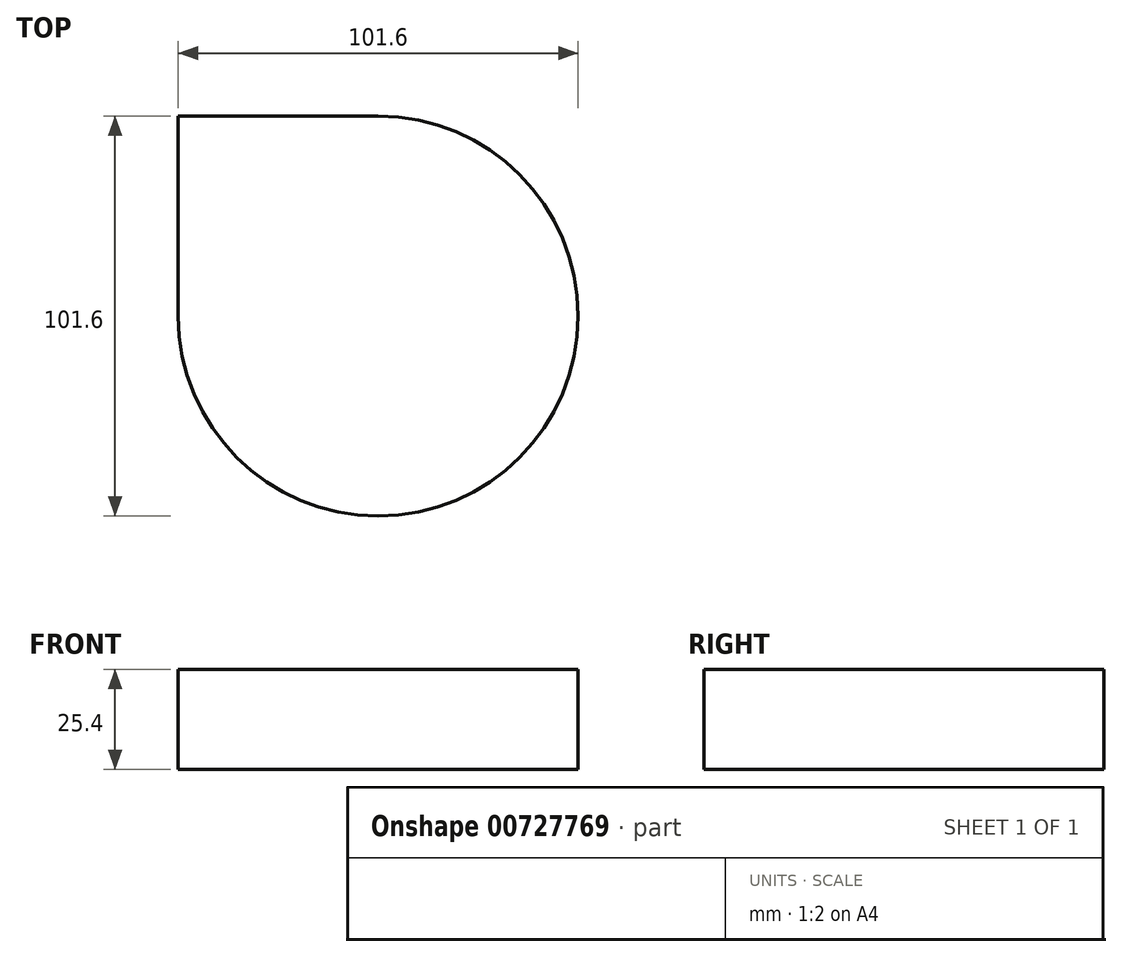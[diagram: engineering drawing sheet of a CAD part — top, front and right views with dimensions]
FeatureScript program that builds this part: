
annotation { "Feature Type Name" : "Feature", "Feature Type Description" : "" }
export const myFeature = defineFeature(function(context is Context, id is Id, definition is map)
    precondition{}
    {
        {
            var Q0;
            Q0=qCreatedBy(makeId("Top.planeOp"),FACE);
            var sketch = newSketch(context, id + "F0", { "sketchPlane" : qUnion([Q0])});
            skLineSegment(sketch, "E0.bottom", {"start": v(-19.57, 32.34) * mm, "end": v(31.23, 32.34) * mm});
            skLineSegment(sketch, "E0.top", {"start": v(-19.57, -18.46) * mm, "end": v(31.23, -18.46) * mm});
            skLineSegment(sketch, "E0.left", {"start": v(-19.57, 32.34) * mm, "end": v(-19.57, -18.46) * mm});
            skLineSegment(sketch, "E0.right", {"start": v(31.23, 32.34) * mm, "end": v(31.23, -18.46) * mm});
            skSolve(sketch);
        }
        {
            var Q0;
            Q0=makeQuery(id+"F0.imprint","IMPRINT",FACE,{"disambiguationData":[TD([[makeQuery(id+"F0.imprint","IMPRINT",EDGE,{"derivedFrom":sQuery(id+"F0.wireOp",EDGE,"E0.bottom")}),-1.0]])]});
            extrude(context, id + "F1", {"entities" : qUnion([Q0]), "depth" : 25.4 * mm, "offsetDistance" : 25.4 * mm});
        }
        {
            var Q0;
            Q0=makeQuery(id+"F1.opExtrude","SWEPT_FACE",FACE,{"disambiguationData":[OSD([sQuery(id+"F0.wireOp",EDGE,"E0.top")])]});
            var Q1;
            Q1=makeQuery(id+"F1.opExtrude","SWEPT_FACE",FACE,{"disambiguationData":[OSD([sQuery(id+"F0.wireOp",EDGE,"E0.right")])]});
            var Q2;
            Q2=makeQuery(id+"F1.opExtrude","SWEPT_EDGE",EDGE,{"disambiguationData":[OSD([sQuery(id+"F0.wireOp",EDGE,"E0.top"),sQuery(id+"F0.wireOp",EDGE,"E0.right")])]});
            revolve(context, id + "F2", {"operationType" : NewBodyOperationType.ADD, "surfaceOperationType" : NewSurfaceOperationType.NEW, "entities" : qUnion([Q0, Q1]), "axis" : qUnion([Q2]), "revolveType" : RevolveType.FULL});
        }
    });
